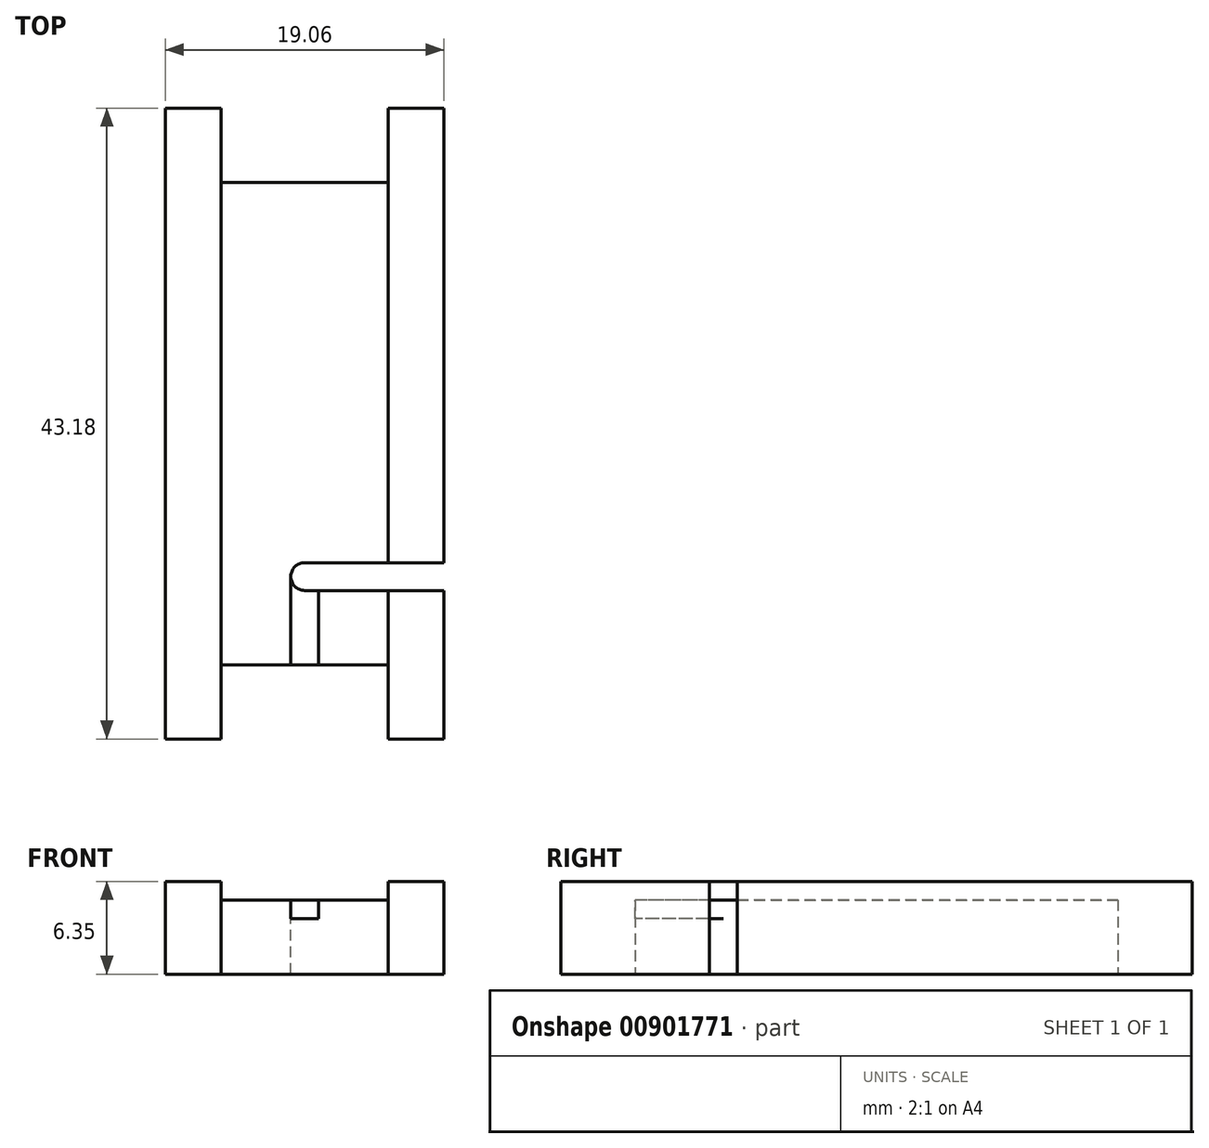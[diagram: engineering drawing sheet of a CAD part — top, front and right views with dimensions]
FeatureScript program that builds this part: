
annotation { "Feature Type Name" : "Feature", "Feature Type Description" : "" }
export const myFeature = defineFeature(function(context is Context, id is Id, definition is map)
    precondition{}
    {
        {
            var Q0;
            Q0=qCreatedBy(makeId("Top.planeOp"),FACE);
            var sketch = newSketch(context, id + "F0", { "sketchPlane" : qUnion([Q0])});
            skLineSegment(sketch, "E0.bottom", {"start": v(9.52, 16.51) * mm, "end": v(-9.53, 16.51) * mm});
            skLineSegment(sketch, "E0.top", {"start": v(9.52, -16.51) * mm, "end": v(-9.53, -16.51) * mm});
            skLineSegment(sketch, "E0.left", {"start": v(9.52, 16.51) * mm, "end": v(9.52, -16.51) * mm});
            skLineSegment(sketch, "E0.right", {"start": v(-9.53, 16.51) * mm, "end": v(-9.53, -16.51) * mm});
            skPoint(sketch, "E0.middle", {"position": v(0, 0) * mm});
            skSolve(sketch);
        }
        {
            var Q0;
            Q0=makeQuery(id+"F0.imprint","IMPRINT",FACE,{"disambiguationData":[TD([[makeQuery(id+"F0.imprint","IMPRINT",EDGE,{"derivedFrom":sQuery(id+"F0.wireOp",EDGE,"E0.bottom")}),1.0]])]});
            extrude(context, id + "F1", {"entities" : qUnion([Q0]), "depth" : 6.35 * mm, "offsetDistance" : 25.4 * mm});
        }
        {
            var Q0;
            Q0=makeQuery(id+"F1.opExtrude","SWEPT_FACE",FACE,{"disambiguationData":[OSD([sQuery(id+"F0.wireOp",EDGE,"E0.top")])]});
            var sketch = newSketch(context, id + "F2", { "sketchPlane" : qUnion([Q0])});
            skLineSegment(sketch, "E1.bottom", {"start": v(-9.53, 6.35) * mm, "end": v(-5.72, 6.35) * mm});
            skLineSegment(sketch, "E1.top", {"start": v(-9.53, 0) * mm, "end": v(-5.72, 0) * mm});
            skLineSegment(sketch, "E1.left", {"start": v(-9.53, 6.35) * mm, "end": v(-9.53, 0) * mm});
            skLineSegment(sketch, "E1.right", {"start": v(-5.72, 6.35) * mm, "end": v(-5.72, 0) * mm});
            skLineSegment(sketch, "E2.bottom", {"start": v(9.52, 6.35) * mm, "end": v(5.71, 6.35) * mm});
            skLineSegment(sketch, "E2.top", {"start": v(9.52, 0) * mm, "end": v(5.71, 0) * mm});
            skLineSegment(sketch, "E2.left", {"start": v(9.52, 6.35) * mm, "end": v(9.52, 0) * mm});
            skLineSegment(sketch, "E2.right", {"start": v(5.71, 6.35) * mm, "end": v(5.71, 0) * mm});
            skSolve(sketch);
        }
        {
            var Q0;
            Q0=makeQuery(id+"F2.imprint","IMPRINT",FACE,{"disambiguationData":[TD([[makeQuery(id+"F2.imprint","IMPRINT",EDGE,{"derivedFrom":sQuery(id+"F2.wireOp",EDGE,"E1.bottom")}),1.0]])]});
            var Q1;
            Q1=makeQuery(id+"F2.imprint","IMPRINT",FACE,{"disambiguationData":[TD([[makeQuery(id+"F2.imprint","IMPRINT",EDGE,{"derivedFrom":sQuery(id+"F2.wireOp",EDGE,"E2.bottom")}),1.0]])]});
            extrude(context, id + "F3", {"entities" : qUnion([Q0, Q1]), "operationType" : NewBodyOperationType.ADD, "depth" : 5.08 * mm, "offsetDistance" : 25.4 * mm});
        }
        {
            var Q0;
            Q0=makeQuery(id+"F1.opExtrude","SWEPT_FACE",FACE,{"disambiguationData":[OSD([sQuery(id+"F0.wireOp",EDGE,"E0.bottom")])]});
            var sketch = newSketch(context, id + "F4", { "sketchPlane" : qUnion([Q0])});
            skLineSegment(sketch, "E3.bottom", {"start": v(-9.52, 6.35) * mm, "end": v(-5.71, 6.35) * mm});
            skLineSegment(sketch, "E3.top", {"start": v(-9.52, 0) * mm, "end": v(-5.71, 0) * mm});
            skLineSegment(sketch, "E3.left", {"start": v(-9.52, 6.35) * mm, "end": v(-9.52, 0) * mm});
            skLineSegment(sketch, "E3.right", {"start": v(-5.71, 6.35) * mm, "end": v(-5.71, 0) * mm});
            skLineSegment(sketch, "E4.bottom", {"start": v(9.53, 6.35) * mm, "end": v(5.72, 6.35) * mm});
            skLineSegment(sketch, "E4.top", {"start": v(9.53, 0) * mm, "end": v(5.72, 0) * mm});
            skLineSegment(sketch, "E4.left", {"start": v(9.53, 6.35) * mm, "end": v(9.53, 0) * mm});
            skLineSegment(sketch, "E4.right", {"start": v(5.72, 6.35) * mm, "end": v(5.72, 0) * mm});
            skSolve(sketch);
        }
        {
            var Q0;
            Q0=makeQuery(id+"F4.imprint","IMPRINT",FACE,{"disambiguationData":[TD([[makeQuery(id+"F4.imprint","IMPRINT",EDGE,{"derivedFrom":sQuery(id+"F4.wireOp",EDGE,"E3.bottom")}),-1.0]])]});
            var Q1;
            Q1=makeQuery(id+"F4.imprint","IMPRINT",FACE,{"disambiguationData":[TD([[makeQuery(id+"F4.imprint","IMPRINT",EDGE,{"derivedFrom":sQuery(id+"F4.wireOp",EDGE,"E4.bottom")}),-1.0]])]});
            extrude(context, id + "F5", {"entities" : qUnion([Q0, Q1]), "operationType" : NewBodyOperationType.ADD, "depth" : 5.08 * mm, "offsetDistance" : 25.4 * mm});
        }
        {
            var Q0;
            Q0=makeQuery(id+"F5.boolean.opBoolean","MERGE",FACE,{"derivedFrom":[makeQuery(id+"F3.boolean.opBoolean","MERGE",FACE,{"derivedFrom":[makeQuery(id+"F1.opExtrude","CAP_FACE",FACE,{"disambiguationData":[OSD([sQuery(id+"F0.wireOp",EDGE,"E0.bottom"),sQuery(id+"F0.wireOp",EDGE,"E0.top"),sQuery(id+"F0.wireOp",EDGE,"E0.left"),sQuery(id+"F0.wireOp",EDGE,"E0.right")])],"isStart":false}),makeQuery(id+"F3.opExtrude","SWEPT_FACE",FACE,{"disambiguationData":[OSD([sQuery(id+"F2.wireOp",EDGE,"E1.bottom")])]}),makeQuery(id+"F3.opExtrude","SWEPT_FACE",FACE,{"disambiguationData":[OSD([sQuery(id+"F2.wireOp",EDGE,"E2.bottom")])]})]}),makeQuery(id+"F5.opExtrude","SWEPT_FACE",FACE,{"disambiguationData":[OSD([sQuery(id+"F4.wireOp",EDGE,"E3.bottom")])]}),makeQuery(id+"F5.opExtrude","SWEPT_FACE",FACE,{"disambiguationData":[OSD([sQuery(id+"F4.wireOp",EDGE,"E4.bottom")])]})]});
            var sketch = newSketch(context, id + "F6", { "sketchPlane" : qUnion([Q0])});
            skLineSegment(sketch, "E5", {"start": v(5.71, -16.51) * mm, "end": v(5.71, 16.51) * mm});
            skLineSegment(sketch, "E6", {"start": v(-5.72, 16.51) * mm, "end": v(-5.72, -16.51) * mm});
            skLineSegment(sketch, "E7.bottom", {"start": v(0, -9.53) * mm, "end": v(9.52, -9.53) * mm});
            skLineSegment(sketch, "E7.top", {"start": v(0, -11.43) * mm, "end": v(9.52, -11.43) * mm});
            skLineSegment(sketch, "E7.left", {"start": v(0, -9.53) * mm, "end": v(0, -11.43) * mm});
            skLineSegment(sketch, "E7.right", {"start": v(9.52, -9.53) * mm, "end": v(9.52, -11.43) * mm});
            skCircle(sketch, "E8", {"center": v(0, -10.48) * mm, "radius": 0.95 * mm});
            skLineSegment(sketch, "E9.bottom", {"start": v(0.95, -10.48) * mm, "end": v(-0.95, -10.48) * mm});
            skLineSegment(sketch, "E9.top", {"start": v(0.95, -16.51) * mm, "end": v(-0.95, -16.51) * mm});
            skLineSegment(sketch, "E9.left", {"start": v(0.95, -10.48) * mm, "end": v(0.95, -16.51) * mm});
            skLineSegment(sketch, "E9.right", {"start": v(-0.95, -10.48) * mm, "end": v(-0.95, -16.51) * mm});
            skSolve(sketch);
        }
        {
            var Q0;
            {var subQ1=sQuery(id+"F6.wireOp",EDGE,"E9.top");Q0=makeQuery(id+"F6.imprint","IMPRINT",FACE,{"disambiguationData":[TD([[makeQuery(id+"F6.imprint","IMPRINT",EDGE,{"derivedFrom":subQ1}),-1.0]])]});}
            var Q1;
            {var subQ1=sQuery(id+"F6.wireOp",EDGE,"E7.top");var subQ3=sQuery(id+"F6.wireOp",EDGE,"E9.left");var subQ4=makeQuery(id+"F6.imprint","INTERSECT",VERTEX,{"derivedFrom":[subQ1,subQ3]});Q1=makeQuery(id+"F6.imprint","IMPRINT",FACE,{"disambiguationData":[TD([[makeQuery(id+"F6.imprint","IMPRINT",EDGE,{"disambiguationData":[TD([[subQ4,1.0]])],"derivedFrom":subQ1}),1.0]])]});}
            extrude(context, id + "F7", {"entities" : qUnion([Q0, Q1]), "operationType" : NewBodyOperationType.REMOVE, "oppositeDirection" : true, "depth" : 2.54 * mm, "offsetDistance" : 25.4 * mm});
        }
        {
            var Q0;
            {var subQ0=sQuery(id+"F6.wireOp",EDGE,"E7.left");Q0=makeQuery(id+"F6.imprint","IMPRINT",FACE,{"disambiguationData":[TD([[makeQuery(id+"F6.imprint","IMPRINT",EDGE,{"derivedFrom":subQ0}),-1.0]])]});}
            var Q1;
            {var subQ0=sQuery(id+"F6.wireOp",EDGE,"E7.left");Q1=makeQuery(id+"F6.imprint","IMPRINT",FACE,{"disambiguationData":[TD([[makeQuery(id+"F6.imprint","IMPRINT",EDGE,{"derivedFrom":subQ0}),1.0]])]});}
            var Q2;
            {var subQ0=sQuery(id+"F6.wireOp",EDGE,"E7.top");var subQ1=sQuery(id+"F6.wireOp",EDGE,"E5");var subQ2=makeQuery(id+"F6.imprint","INTERSECT",VERTEX,{"derivedFrom":[subQ1,subQ0]});Q2=makeQuery(id+"F6.imprint","IMPRINT",FACE,{"disambiguationData":[TD([[makeQuery(id+"F6.imprint","IMPRINT",EDGE,{"disambiguationData":[TD([[subQ2,-1.0]])],"derivedFrom":subQ1}),1.0]])]});}
            var Q3;
            {var subQ5=sQuery(id+"F6.wireOp",EDGE,"E7.right");Q3=makeQuery(id+"F6.imprint","IMPRINT",FACE,{"disambiguationData":[TD([[makeQuery(id+"F6.imprint","IMPRINT",EDGE,{"derivedFrom":subQ5}),-1.0]])]});}
            var Q4;
            {var subQ1=sQuery(id+"F6.wireOp",EDGE,"E7.top");var subQ3=sQuery(id+"F6.wireOp",EDGE,"E9.left");var subQ4=makeQuery(id+"F6.imprint","INTERSECT",VERTEX,{"derivedFrom":[subQ1,subQ3]});Q4=makeQuery(id+"F6.imprint","IMPRINT",FACE,{"disambiguationData":[TD([[makeQuery(id+"F6.imprint","IMPRINT",EDGE,{"disambiguationData":[TD([[subQ4,1.0]])],"derivedFrom":subQ1}),1.0]])]});}
            extrude(context, id + "F8", {"entities" : qUnion([Q0, Q1, Q2, Q3, Q4]), "operationType" : NewBodyOperationType.REMOVE, "oppositeDirection" : true, "depth" : 6.35 * mm, "offsetDistance" : 25.4 * mm});
        }
        {
            var Q0;
            {var subQ8=sQuery(id+"F6.wireOp",EDGE,"E6");Q0=makeQuery(id+"F6.imprint","IMPRINT",FACE,{"disambiguationData":[TD([[makeQuery(id+"F6.imprint","IMPRINT",EDGE,{"derivedFrom":subQ8}),1.0]])]});}
            var Q1;
            {var subQ0=sQuery(id+"F6.wireOp",EDGE,"E5");var subQ4=sQuery(id+"F6.wireOp",EDGE,"E7.top");var subQ5=makeQuery(id+"F6.imprint","INTERSECT",VERTEX,{"derivedFrom":[subQ0,subQ4]});Q1=makeQuery(id+"F6.imprint","IMPRINT",FACE,{"disambiguationData":[TD([[makeQuery(id+"F6.imprint","IMPRINT",EDGE,{"disambiguationData":[TD([[subQ5,1.0]])],"derivedFrom":subQ4}),-1.0]])]});}
            extrude(context, id + "F9", {"entities" : qUnion([Q0, Q1]), "operationType" : NewBodyOperationType.REMOVE, "oppositeDirection" : true, "depth" : 1.27 * mm, "offsetDistance" : 25.4 * mm});
        }
    });
